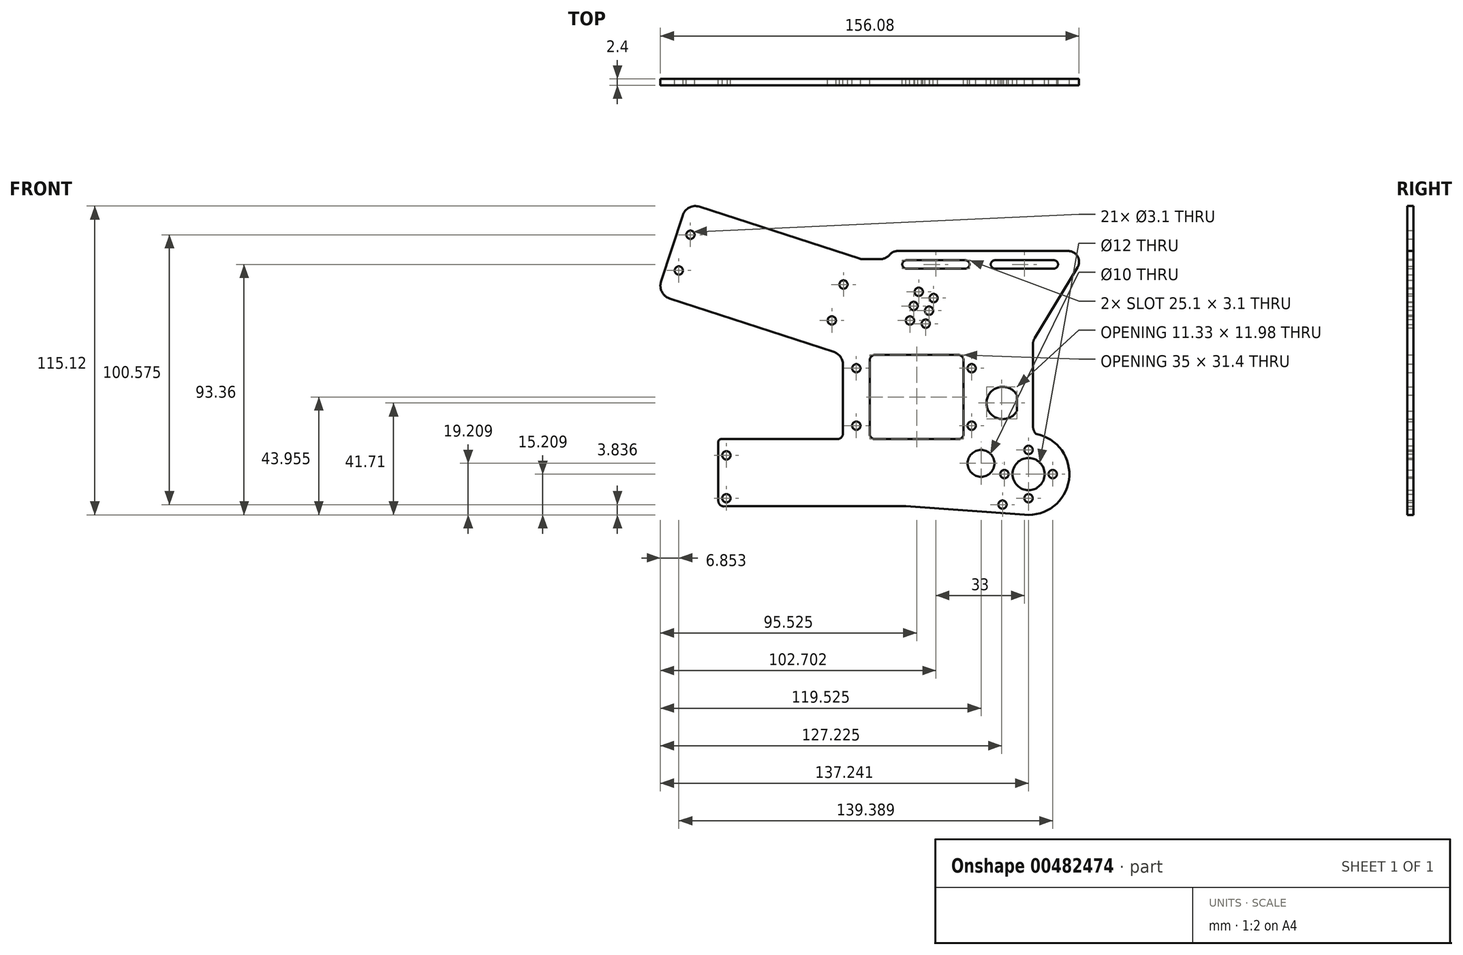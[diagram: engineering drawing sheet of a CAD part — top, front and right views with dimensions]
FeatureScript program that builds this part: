
annotation { "Feature Type Name" : "Feature", "Feature Type Description" : "" }
export const myFeature = defineFeature(function(context is Context, id is Id, definition is map)
    precondition{}
    {
        {
            var Q0;
            Q0=qCreatedBy(makeId("Front.planeOp"),FACE);
            var sketch = newSketch(context, id + "F0", { "sketchPlane" : qUnion([Q0])});
            skLineSegment(sketch, "E0.bottom", {"start": v(-108.02, -14.6) * mm, "end": v(-12.02, -14.6) * mm, "construction": true});
            skLineSegment(sketch, "E0.top", {"start": v(-108.02, -61.1) * mm, "end": v(-12.02, -61.1) * mm, "construction": true});
            skLineSegment(sketch, "E0.left", {"start": v(-108.02, -14.6) * mm, "end": v(-108.02, -61.1) * mm, "construction": true});
            skLineSegment(sketch, "E0.right", {"start": v(-12.02, -14.6) * mm, "end": v(-12.02, -61.1) * mm, "construction": true});
            skLineSegment(sketch, "E1", {"start": v(-112.52, -36.6) * mm, "end": v(-45.97, -36.6) * mm});
            skLineSegment(sketch, "E2", {"start": v(-136.99, 48.08) * mm, "end": v(-115.36, 41.05) * mm});
            skLineSegment(sketch, "E3", {"start": v(-115.36, 41.05) * mm, "end": v(-81.75, 30.13) * mm});
            skPoint(sketch, "E4", {"position": v(-0.3, -24.6) * mm});
            skLineSegment(sketch, "E5", {"start": v(-137.3, 47.12) * mm, "end": v(-129.26, 71.85) * mm});
            skLineSegment(sketch, "E6", {"start": v(-57.52, -11.55) * mm, "end": v(-26.52, -11.55) * mm});
            skLineSegment(sketch, "E7", {"start": v(-24.52, -9.55) * mm, "end": v(-24.52, 17.84) * mm});
            skCircle(sketch, "E8", {"center": v(-0.3, -24.6) * mm, "radius": 6 * mm});
            skLineSegment(sketch, "E9", {"start": v(-59.52, -9.55) * mm, "end": v(-59.52, 17.84) * mm});
            skLineSegment(sketch, "E10", {"start": v(2.03, 26.1) * mm, "end": v(18.16, 52.81) * mm});
            skLineSegment(sketch, "E11", {"start": v(-4.65, 4.9) * mm, "end": v(-4.65, -1.1) * mm});
            skArc(sketch, "E12", {"start": v(-4.65, 4.9) * mm, "mid": v(-15.85, 1.9) * mm, "end": v(-4.65, -1.1) * mm});
            skLineSegment(sketch, "E13", {"start": v(1.3, -6.42) * mm, "end": v(1.3, 23.52) * mm});
            skLineSegment(sketch, "E14.trimOffspring", {"start": v(2.14, -9.2) * mm, "end": v(2.38, -9.55) * mm});
            skLineSegment(sketch, "E15", {"start": v(-74.52, -11.55) * mm, "end": v(-112.52, -11.55) * mm});
            skLineSegment(sketch, "E16", {"start": v(-134.09, 40.82) * mm, "end": v(-72.97, 20.97) * mm});
            skLineSegment(sketch, "E17", {"start": v(-69.52, 16.21) * mm, "end": v(-69.52, -9.55) * mm});
            skLineSegment(sketch, "E18", {"start": v(-74.52, -11.55) * mm, "end": v(-71.52, -11.55) * mm});
            skLineSegment(sketch, "E19", {"start": v(-57.52, 19.84) * mm, "end": v(-26.52, 19.84) * mm});
            skLineSegment(sketch, "E20", {"start": v(-74.33, 52.95) * mm, "end": v(-129.57, 70.9) * mm});
            skLineSegment(sketch, "E21", {"start": v(-122.96, 75.06) * mm, "end": v(-72.48, 58.66) * mm});
            skLineSegment(sketch, "E22", {"start": v(-72.48, 58.66) * mm, "end": v(-63.45, 55.73) * mm});
            skLineSegment(sketch, "E23", {"start": v(-61.9, 55.48) * mm, "end": v(-55.82, 55.48) * mm});
            skLineSegment(sketch, "E24", {"start": v(-52.12, 57.12) * mm, "end": v(-52, 57.24) * mm});
            skLineSegment(sketch, "E25", {"start": v(-28.73, 58.55) * mm, "end": v(-32.7, 52) * mm, "construction": true});
            skPoint(sketch, "E26", {"position": v(-130.69, 51.29) * mm});
            skPoint(sketch, "E27", {"position": v(-126.36, 64.6) * mm});
            skLineSegment(sketch, "E28", {"start": v(-74.33, 52.95) * mm, "end": v(-68.5, 51.06) * mm});
            skLineSegment(sketch, "E29", {"start": v(-75.94, 28.15) * mm, "end": v(-81.75, 30.13) * mm});
            skLineSegment(sketch, "E30", {"start": v(-68.5, 51.06) * mm, "end": v(-63, 49.27) * mm});
            skLineSegment(sketch, "E31", {"start": v(-63, 49.27) * mm, "end": v(-70.44, 26.36) * mm});
            skLineSegment(sketch, "E32", {"start": v(-75.94, 28.15) * mm, "end": v(-70.44, 26.36) * mm});
            skPoint(sketch, "E33", {"position": v(-69.3, 46.06) * mm});
            skPoint(sketch, "E34", {"position": v(-73.65, 32.66) * mm});
            skCircle(sketch, "E35", {"center": v(-18.02, -20.6) * mm, "radius": 5 * mm});
            skPoint(sketch, "E36", {"position": v(-96.28, 60.09) * mm});
            skPoint(sketch, "E37", {"position": v(-103.7, 37.26) * mm});
            skLineSegment(sketch, "E38", {"start": v(-96.28, 60.09) * mm, "end": v(-92.82, 70.75) * mm, "construction": true});
            skLineSegment(sketch, "E39", {"start": v(-92.82, 70.75) * mm, "end": v(-106.39, 29) * mm, "construction": true});
            skPoint(sketch, "E40.visualSharp", {"position": v(-24.52, 19.84) * mm});
            skArc(sketch, "E40.filletArc", {"start": v(-24.52, 17.84) * mm, "mid": v(-25.1, 19.26) * mm, "end": v(-26.52, 19.84) * mm});
            skPoint(sketch, "E41.visualSharp", {"position": v(-59.52, 19.84) * mm});
            skArc(sketch, "E41.filletArc", {"start": v(-57.52, 19.84) * mm, "mid": v(-58.93, 19.26) * mm, "end": v(-59.52, 17.84) * mm});
            skPoint(sketch, "E42.visualSharp", {"position": v(-24.52, -11.55) * mm});
            skArc(sketch, "E42.filletArc", {"start": v(-26.52, -11.55) * mm, "mid": v(-25.1, -10.97) * mm, "end": v(-24.52, -9.55) * mm});
            skPoint(sketch, "E43.visualSharp", {"position": v(-59.52, -11.55) * mm});
            skArc(sketch, "E43.filletArc", {"start": v(-59.52, -9.55) * mm, "mid": v(-58.93, -10.97) * mm, "end": v(-57.52, -11.55) * mm});
            skPoint(sketch, "E44.visualSharp", {"position": v(-114.52, -11.55) * mm});
            skArc(sketch, "E44.filletArc", {"start": v(-112.52, -11.55) * mm, "mid": v(-112.53, -11.55) * mm, "end": v(-112.54, -11.55) * mm});
            skPoint(sketch, "E45.visualSharp", {"position": v(-69.52, -11.55) * mm});
            skArc(sketch, "E45.filletArc", {"start": v(-71.52, -11.55) * mm, "mid": v(-70.1, -10.97) * mm, "end": v(-69.52, -9.55) * mm});
            skPoint(sketch, "E46.visualSharp", {"position": v(-69.52, 19.84) * mm});
            skArc(sketch, "E46.filletArc", {"start": v(-69.52, 16.21) * mm, "mid": v(-70.47, 19.15) * mm, "end": v(-72.97, 20.97) * mm});
            skPoint(sketch, "E47.visualSharp", {"position": v(-138.84, 42.37) * mm});
            skArc(sketch, "E47.filletArc", {"start": v(-137.3, 47.12) * mm, "mid": v(-137, 43.3) * mm, "end": v(-134.09, 40.82) * mm});
            skPoint(sketch, "E48.visualSharp", {"position": v(-127.72, 76.6) * mm});
            skArc(sketch, "E48.filletArc", {"start": v(-122.96, 75.06) * mm, "mid": v(-126.78, 74.76) * mm, "end": v(-129.26, 71.85) * mm});
            skPoint(sketch, "E49.visualSharp", {"position": v(1.3, 24.91) * mm});
            skArc(sketch, "E49.filletArc", {"start": v(2.03, 26.1) * mm, "mid": v(1.49, 24.86) * mm, "end": v(1.3, 23.52) * mm});
            skPoint(sketch, "E50.visualSharp", {"position": v(1.3, -7.93) * mm});
            skArc(sketch, "E50.filletArc", {"start": v(1.3, -6.42) * mm, "mid": v(1.52, -7.87) * mm, "end": v(2.14, -9.2) * mm});
            skPoint(sketch, "E51.visualSharp", {"position": v(2.44, -9.64) * mm});
            skArc(sketch, "E51.filletArc", {"start": v(2.38, -9.55) * mm, "mid": v(2.45, -9.62) * mm, "end": v(2.55, -9.66) * mm});
            skPoint(sketch, "E52.visualSharp", {"position": v(-114.52, -36.6) * mm});
            skPoint(sketch, "E53.visualSharp", {"position": v(-53.6, 55.48) * mm});
            skArc(sketch, "E53.filletArc", {"start": v(-55.82, 55.48) * mm, "mid": v(-53.8, 55.9) * mm, "end": v(-52.12, 57.12) * mm});
            skPoint(sketch, "E54.visualSharp", {"position": v(-62.7, 55.48) * mm});
            skArc(sketch, "E54.filletArc", {"start": v(-63.45, 55.73) * mm, "mid": v(-62.69, 55.54) * mm, "end": v(-61.9, 55.48) * mm});
            skCircle(sketch, "E55", {"center": v(-112.96, -17.6) * mm, "radius": 1.55 * mm});
            skCircle(sketch, "E56", {"center": v(-112.96, -33.6) * mm, "radius": 1.55 * mm});
            skLineSegment(sketch, "E57", {"start": v(-71.52, -11.55) * mm, "end": v(-57.52, -11.55) * mm, "construction": true});
            skCircle(sketch, "E58", {"center": v(-64.52, -6.55) * mm, "radius": 1.55 * mm});
            skPoint(sketch, "E58.centerSnap0", {"position": v(-64.52, -11.55) * mm});
            skLineSegment(sketch, "E59", {"start": v(-57.52, 19.84) * mm, "end": v(-71.08, 19.84) * mm, "construction": true});
            skCircle(sketch, "E60", {"center": v(-64.52, 14.84) * mm, "radius": 1.55 * mm});
            skLineSegment(sketch, "E61", {"start": v(-64.52, 14.84) * mm, "end": v(-17.25, 14.84) * mm, "construction": true});
            skLineSegment(sketch, "E62", {"start": v(-64.52, -6.55) * mm, "end": v(-17, -6.55) * mm, "construction": true});
            skCircle(sketch, "E63", {"center": v(-21.52, 14.84) * mm, "radius": 1.55 * mm});
            skCircle(sketch, "E64", {"center": v(-21.52, -6.55) * mm, "radius": 1.55 * mm});
            skLineSegment(sketch, "E65", {"start": v(-1.76, -39.74) * mm, "end": v(-45.97, -36.6) * mm});
            skCircle(sketch, "E66", {"center": v(-10.02, -35.97) * mm, "radius": 3 * mm, "construction": true});
            skArc(sketch, "E67.trimOffspring", {"start": v(-1.76, -39.74) * mm, "mid": v(14.76, -26.76) * mm, "end": v(2.55, -9.66) * mm});
            skCircle(sketch, "E68", {"center": v(-10.02, -35.97) * mm, "radius": 1.55 * mm});
            skLineSegment(sketch, "E69", {"start": v(-115.96, -12.57) * mm, "end": v(-115.96, -34.62) * mm});
            skLineSegment(sketch, "E70", {"start": v(-113.92, -36.62) * mm, "end": v(-112.52, -36.6) * mm});
            skLineSegment(sketch, "E71", {"start": v(-114.96, -11.57) * mm, "end": v(-112.52, -11.55) * mm});
            skPoint(sketch, "E72.visualSharp", {"position": v(-115.96, -11.58) * mm});
            skArc(sketch, "E72.filletArc", {"start": v(-114.96, -11.57) * mm, "mid": v(-115.66, -11.86) * mm, "end": v(-115.96, -12.57) * mm});
            skPoint(sketch, "E73.visualSharp", {"position": v(-115.96, -36.66) * mm});
            skArc(sketch, "E73.filletArc", {"start": v(-115.96, -34.62) * mm, "mid": v(-115.36, -36.05) * mm, "end": v(-113.92, -36.62) * mm});
            skCircle(sketch, "E74", {"center": v(-126.36, 64.6) * mm, "radius": 1.55 * mm});
            skCircle(sketch, "E75", {"center": v(-130.69, 51.29) * mm, "radius": 1.55 * mm});
            skCircle(sketch, "E76", {"center": v(-69.3, 46.06) * mm, "radius": 1.55 * mm});
            skCircle(sketch, "E77", {"center": v(-73.65, 32.66) * mm, "radius": 1.55 * mm});
            skArc(sketch, "E78", {"start": v(8.7, -24.6) * mm, "mid": v(6.59, -18.8) * mm, "end": v(1.25, -15.73) * mm, "construction": true});
            skCircle(sketch, "E79", {"center": v(-9.3, -24.6) * mm, "radius": 1.55 * mm});
            skCircle(sketch, "E80", {"center": v(-0.3, -15.6) * mm, "radius": 1.55 * mm});
            skCircle(sketch, "E81", {"center": v(8.7, -24.6) * mm, "radius": 1.55 * mm});
            skCircle(sketch, "E82", {"center": v(-0.3, -33.6) * mm, "radius": 1.55 * mm});
            skPoint(sketch, "E83.start.orphan", {"position": v(-122.72, 43.44) * mm});
            skPoint(sketch, "E84.end.orphan", {"position": v(-104.5, 34.79) * mm});
            skPoint(sketch, "E84.start.orphan", {"position": v(-123.53, 40.97) * mm});
            skPoint(sketch, "E85.MirrorCS.start.orphan", {"position": v(-85.48, 28.6) * mm});
            skPoint(sketch, "E86.MirrorCS.start.orphan", {"position": v(-84.68, 31.08) * mm});
            skPoint(sketch, "E87.end.orphan", {"position": v(-95.48, 62.56) * mm});
            skPoint(sketch, "E88.end.orphan", {"position": v(-114.5, 68.74) * mm});
            skPoint(sketch, "E88.start.orphan", {"position": v(-115.3, 66.27) * mm});
            skPoint(sketch, "E89.MirrorCS.start.orphan", {"position": v(-76.46, 56.38) * mm});
            skPoint(sketch, "E90.MirrorCS.start.orphan", {"position": v(-77.26, 53.9) * mm});
            skLineSegment(sketch, "E91", {"start": v(-28.73, 58.55) * mm, "end": v(-49.04, 58.55) * mm});
            skLineSegment(sketch, "E92", {"start": v(-28.73, 58.55) * mm, "end": v(14.54, 58.55) * mm});
            skLineSegment(sketch, "E93", {"start": v(17.96, 52.48) * mm, "end": v(18.16, 52.81) * mm});
            skPoint(sketch, "E94.visualSharp", {"position": v(21.63, 58.55) * mm});
            skArc(sketch, "E94.filletArc", {"start": v(17.96, 52.48) * mm, "mid": v(18.02, 56.52) * mm, "end": v(14.54, 58.55) * mm});
            skPoint(sketch, "E95.visualSharp", {"position": v(-50.81, 58.55) * mm});
            skArc(sketch, "E95.filletArc", {"start": v(-49.04, 58.55) * mm, "mid": v(-50.66, 58.2) * mm, "end": v(-52, 57.24) * mm});
            skLineSegment(sketch, "E96", {"start": v(-45.84, 53.55) * mm, "end": v(-23.84, 53.55) * mm, "construction": true});
            skLineSegment(sketch, "E97", {"start": v(-12.84, 53.55) * mm, "end": v(9.16, 53.55) * mm, "construction": true});
            skArc(sketch, "E98.0.startCap", {"start": v(-45.84, 52) * mm, "mid": v(-47.39, 53.55) * mm, "end": v(-45.84, 55.1) * mm});
            skArc(sketch, "E98.0.endCap", {"start": v(-23.84, 55.1) * mm, "mid": v(-22.29, 53.55) * mm, "end": v(-23.84, 52) * mm});
            skLineSegment(sketch, "E98.0.left", {"start": v(-45.84, 55.1) * mm, "end": v(-23.84, 55.1) * mm});
            skLineSegment(sketch, "E98.0.right", {"start": v(-45.84, 52) * mm, "end": v(-23.84, 52) * mm});
            skArc(sketch, "E99.0.startCap", {"start": v(-12.84, 52) * mm, "mid": v(-14.39, 53.55) * mm, "end": v(-12.84, 55.1) * mm});
            skArc(sketch, "E99.0.endCap", {"start": v(9.16, 55.1) * mm, "mid": v(10.71, 53.55) * mm, "end": v(9.16, 52) * mm});
            skLineSegment(sketch, "E99.0.left", {"start": v(-12.84, 55.1) * mm, "end": v(9.16, 55.1) * mm});
            skLineSegment(sketch, "E99.0.right", {"start": v(-12.84, 52) * mm, "end": v(9.16, 52) * mm});
            skLineSegment(sketch, "E100", {"start": v(-24.66, -11.55) * mm, "end": v(-24.66, 19.85) * mm});
            skLineSegment(sketch, "E101", {"start": v(-59.66, -11.55) * mm, "end": v(-59.66, 19.85) * mm});
            skLineSegment(sketch, "E102", {"start": v(-4.79, 4.9) * mm, "end": v(-4.79, -1.1) * mm});
            skArc(sketch, "E103", {"start": v(-4.79, 4.9) * mm, "mid": v(-15.99, 1.9) * mm, "end": v(-4.79, -1.1) * mm});
            skLineSegment(sketch, "E104", {"start": v(-59.66, 19.85) * mm, "end": v(-24.66, 19.85) * mm});
            skPoint(sketch, "E105", {"position": v(-131.03, 51.36) * mm});
            skPoint(sketch, "E106", {"position": v(-126.7, 64.67) * mm});
            skPoint(sketch, "E107", {"position": v(-69.64, 46.13) * mm});
            skPoint(sketch, "E108", {"position": v(-74, 32.74) * mm});
            skLineSegment(sketch, "E109", {"start": v(-24.42, -11.4) * mm, "end": v(-24.42, 19.99) * mm});
            skArc(sketch, "E110", {"start": v(-4.56, 5.04) * mm, "mid": v(-15.76, 2.04) * mm, "end": v(-4.56, -0.96) * mm});
            skLineSegment(sketch, "E111", {"start": v(-138.95, 42.58) * mm, "end": v(-69.42, 19.99) * mm});
            skLineSegment(sketch, "E112", {"start": v(-69.42, 19.99) * mm, "end": v(-69.42, -11.4) * mm});
            skLineSegment(sketch, "E113", {"start": v(-59.42, 19.99) * mm, "end": v(-24.42, 19.99) * mm});
            skCircle(sketch, "E114", {"center": v(-38.63, 31.45) * mm, "radius": 1.55 * mm});
            skCircle(sketch, "E115", {"center": v(-37.4, 36.3) * mm, "radius": 1.55 * mm});
            skCircle(sketch, "E116", {"center": v(-35.7, 41) * mm, "radius": 1.55 * mm});
            skLineSegment(sketch, "E117", {"start": v(11.36, 21.34) * mm, "end": v(-50.86, 27.69) * mm, "construction": true});
            skLineSegment(sketch, "E118", {"start": v(13.17, 20.98) * mm, "end": v(-48.45, 33.43) * mm, "construction": true});
            skLineSegment(sketch, "E119", {"start": v(12.42, 21.02) * mm, "end": v(-45.62, 38.82) * mm, "construction": true});
            skLineSegment(sketch, "E120", {"start": v(11.26, 21.38) * mm, "end": v(-42.03, 43.66) * mm, "construction": true});
            skLineSegment(sketch, "E121", {"start": v(11.36, 21.34) * mm, "end": v(-41.18, 49.62) * mm, "construction": true});
            skCircle(sketch, "E122", {"center": v(-44.51, 32.64) * mm, "radius": 1.55 * mm});
            skCircle(sketch, "E123", {"center": v(-43.14, 38.06) * mm, "radius": 1.55 * mm});
            skCircle(sketch, "E124", {"center": v(-41.23, 43.33) * mm, "radius": 1.55 * mm});
            skSolve(sketch);
        }
        {
            var Q0;
            Q0 = qSketchRegion(id + "F0", true);
            extrude(context, id + "F1", {"entities" : qUnion([Q0]), "depth" : 2.4 * mm, "offsetDistance" : 25 * mm});
        }
    });
